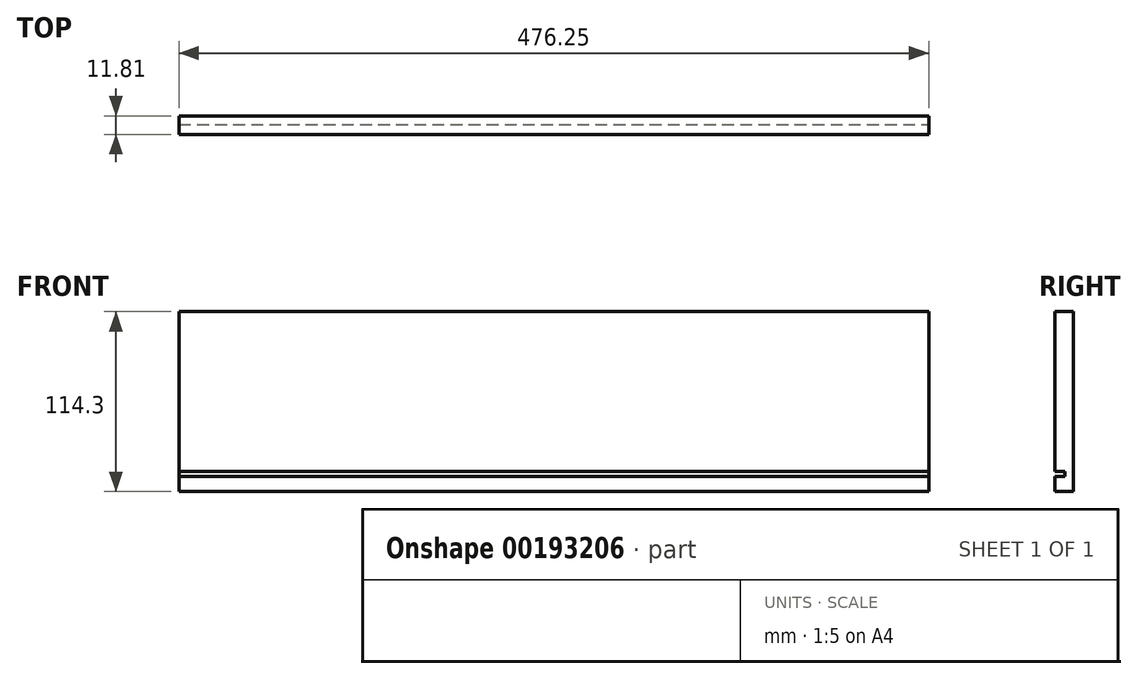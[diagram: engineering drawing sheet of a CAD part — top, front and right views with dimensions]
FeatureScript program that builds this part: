
annotation { "Feature Type Name" : "Feature", "Feature Type Description" : "" }
export const myFeature = defineFeature(function(context is Context, id is Id, definition is map)
    precondition{}
    {
        {
            var Q0;
            Q0=qCreatedBy(makeId("Right.planeOp"),FACE);
            var sketch = newSketch(context, id + "F0", { "sketchPlane" : qUnion([Q0])});
            skLineSegment(sketch, "E0.bottom", {"start": v(0.03, 24.7) * mm, "end": v(11.84, 24.7) * mm});
            skLineSegment(sketch, "E0.top", {"start": v(0.03, -89.6) * mm, "end": v(11.84, -89.6) * mm});
            skLineSegment(sketch, "E0.left", {"start": v(0.03, 24.7) * mm, "end": v(0.03, -76.9) * mm});
            skLineSegment(sketch, "E0.right", {"start": v(11.84, 24.7) * mm, "end": v(11.84, -89.6) * mm});
            skLineSegment(sketch, "E1.bottom", {"start": v(0.03, -76.9) * mm, "end": v(6.38, -76.9) * mm});
            skLineSegment(sketch, "E1.top", {"start": v(0.03, -80.07) * mm, "end": v(6.38, -80.07) * mm});
            skLineSegment(sketch, "E1.right", {"start": v(6.38, -76.9) * mm, "end": v(6.38, -80.07) * mm});
            skLineSegment(sketch, "E2.trimOffspring", {"start": v(0.03, -80.07) * mm, "end": v(0.03, -89.6) * mm});
            skSolve(sketch);
        }
        {
            var Q0;
            Q0 = qSketchRegion(id + "F0", true);
            extrude(context, id + "F1", {"entities" : qUnion([Q0]), "oppositeDirection" : true, "depth" : 476.25 * mm});
        }
    });
